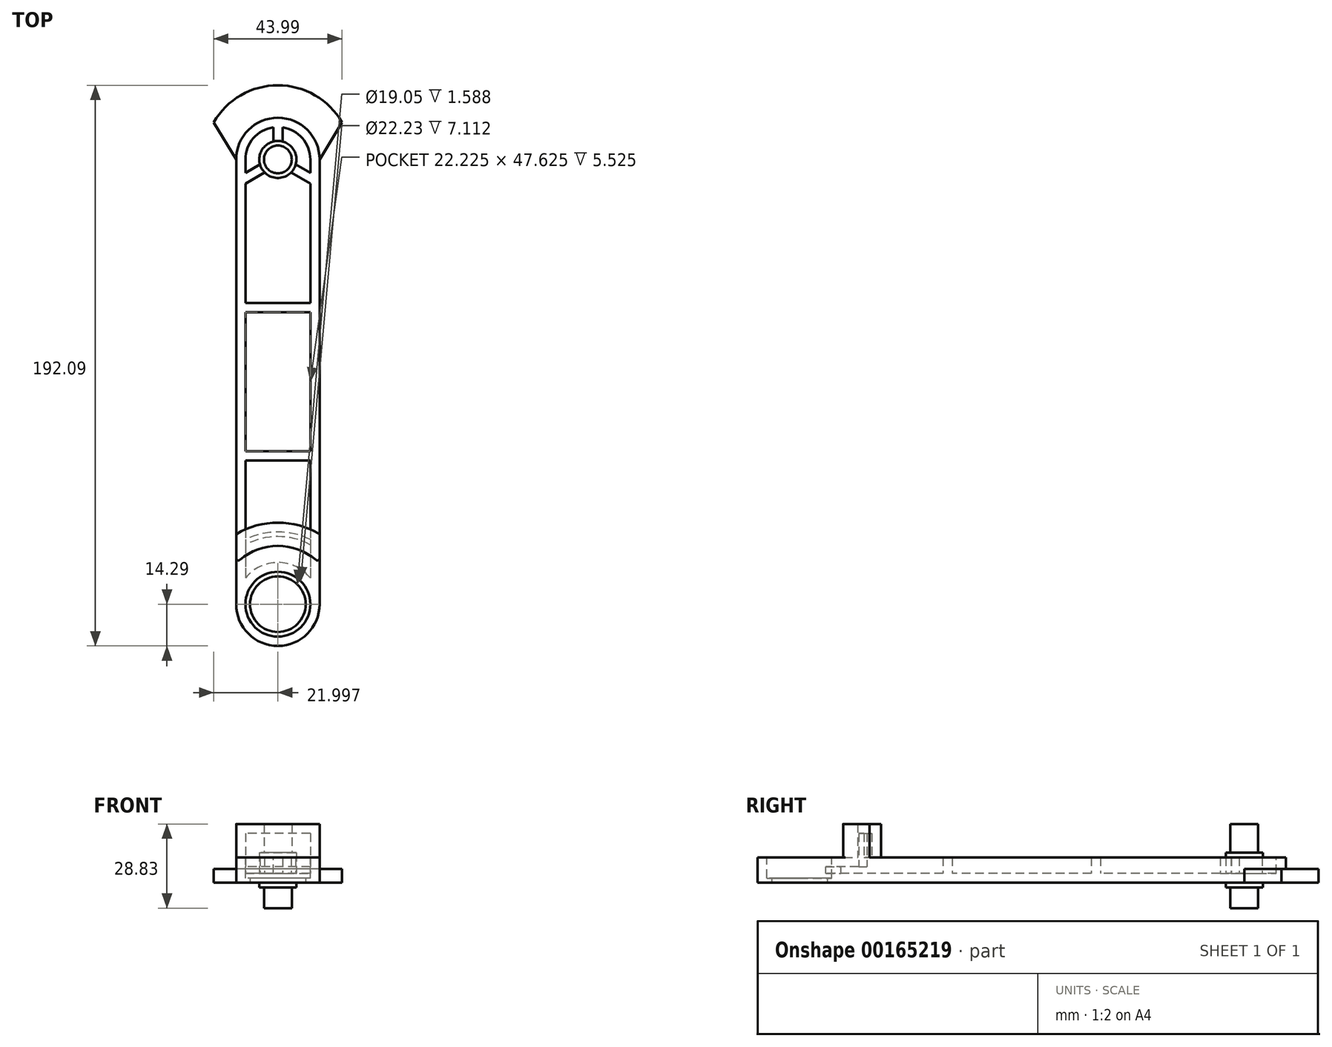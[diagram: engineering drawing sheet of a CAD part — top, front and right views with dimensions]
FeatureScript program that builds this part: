
annotation { "Feature Type Name" : "Feature", "Feature Type Description" : "" }
export const myFeature = defineFeature(function(context is Context, id is Id, definition is map)
    precondition{}
    {
        {
            var Q0;
            Q0=qCreatedBy(makeId("Top.planeOp"),FACE);
            var sketch = newSketch(context, id + "F0", { "sketchPlane" : qUnion([Q0])});
            skLineSegment(sketch, "E0.bottom", {"start": v(0, 0) * mm, "end": v(28.58, 0) * mm, "construction": true});
            skLineSegment(sketch, "E0.top", {"start": v(0, -152.4) * mm, "end": v(28.58, -152.4) * mm, "construction": true});
            skLineSegment(sketch, "E0.left", {"start": v(0, 0) * mm, "end": v(0, -152.4) * mm});
            skLineSegment(sketch, "E0.right", {"start": v(28.58, 0) * mm, "end": v(28.58, -152.4) * mm});
            skArc(sketch, "E1", {"start": v(0, -152.4) * mm, "mid": v(14.29, -166.69) * mm, "end": v(28.58, -152.4) * mm});
            skCircle(sketch, "E2", {"center": v(14.29, -152.4) * mm, "radius": 9.53 * mm});
            skLineSegment(sketch, "E3", {"start": v(0, 0) * mm, "end": v(-7.7, 12.7) * mm});
            skLineSegment(sketch, "E4", {"start": v(-7.7, 12.7) * mm, "end": v(36.28, 12.7) * mm, "construction": true});
            skLineSegment(sketch, "E5", {"start": v(36.28, 12.7) * mm, "end": v(28.57, 0) * mm});
            skLineSegment(sketch, "E6", {"start": v(14.29, 0) * mm, "end": v(14.29, 12.7) * mm, "construction": true});
            skArc(sketch, "E7", {"start": v(36.28, 12.7) * mm, "mid": v(14.29, 25.4) * mm, "end": v(-7.7, 12.7) * mm});
            skLineSegment(sketch, "E8", {"start": v(-7.7, 12.7) * mm, "end": v(14.29, 0) * mm, "construction": true});
            skLineSegment(sketch, "E9", {"start": v(14.29, 0) * mm, "end": v(36.28, 12.7) * mm, "construction": true});
            skSolve(sketch);
        }
        {
            var Q0;
            Q0 = qSketchRegion(id + "F0", true);
            extrude(context, id + "F1", {"entities" : qUnion([Q0]), "depth" : 8.7 * mm});
        }
        {
            var Q0;
            Q0=makeQuery(id+"F1.opExtrude","CAP_FACE",FACE,{"disambiguationData":[OSD([sQuery(id+"F0.wireOp",EDGE,"E0.left"),sQuery(id+"F0.wireOp",EDGE,"E0.right"),sQuery(id+"F0.wireOp",EDGE,"E1"),sQuery(id+"F0.wireOp",EDGE,"bbfeQyJU-4Eoz-mEa2-qj02-75LyADXawIuP"),sQuery(id+"F0.wireOp",EDGE,"E2")])],"isStart":false});
            var sketch = newSketch(context, id + "F2", { "sketchPlane" : qUnion([Q0])});
            skCircle(sketch, "E10", {"center": v(14.29, -152.4) * mm, "radius": 11.11 * mm});
            skSolve(sketch);
        }
        {
            var Q0;
            Q0 = qSketchRegion(id + "F2", true);
            extrude(context, id + "F3", {"entities" : qUnion([Q0]), "operationType" : NewBodyOperationType.REMOVE, "oppositeDirection" : true, "depth" : 7.11 * mm});
        }
        {
            var Q0;
            Q0=makeQuery(id+"F1.opExtrude","CAP_FACE",FACE,{"disambiguationData":[OSD([sQuery(id+"F0.wireOp",EDGE,"E0.left"),sQuery(id+"F0.wireOp",EDGE,"E0.right"),sQuery(id+"F0.wireOp",EDGE,"E1"),sQuery(id+"F0.wireOp",EDGE,"bbfeQyJU-4Eoz-mEa2-qj02-75LyADXawIuP"),sQuery(id+"F0.wireOp",EDGE,"E2")])],"isStart":false});
            var sketch = newSketch(context, id + "F4", { "sketchPlane" : qUnion([Q0])});
            skArc(sketch, "E11", {"start": v(28.57, -138.4) * mm, "mid": v(14.29, -132.39) * mm, "end": v(0, -138.4) * mm});
            skArc(sketch, "E12", {"start": v(28.58, -128.38) * mm, "mid": v(14.29, -124.45) * mm, "end": v(0, -128.38) * mm});
            skLineSegment(sketch, "E13", {"start": v(0, -128.38) * mm, "end": v(0, -138.4) * mm});
            skLineSegment(sketch, "E14", {"start": v(28.58, -128.38) * mm, "end": v(28.58, -138.4) * mm});
            skSolve(sketch);
        }
        {
            var Q0;
            Q0=makeQuery(id+"F4.imprint","IMPRINT",FACE,{"disambiguationData":[TD([[makeQuery(id+"F4.imprint","IMPRINT",EDGE,{"derivedFrom":sQuery(id+"F4.wireOp",EDGE,"E11")}),-1.0]])]});
            extrude(context, id + "F5", {"entities" : qUnion([Q0]), "operationType" : NewBodyOperationType.ADD, "depth" : 11.43 * mm});
        }
        {
            var Q0;
            Q0=makeQuery(id+"F5.opExtrude","SWEPT_EDGE",EDGE,{"disambiguationData":[OSD([sQuery(id+"F0.wireOp",EDGE,"E0.left"),sQuery(id+"F4.wireOp",EDGE,"E11"),sQuery(id+"F4.wireOp",EDGE,"E13")])]});
            var Q1;
            Q1=makeQuery(id+"F5.opExtrude","SWEPT_EDGE",EDGE,{"disambiguationData":[OSD([sQuery(id+"F0.wireOp",EDGE,"E0.right"),sQuery(id+"F4.wireOp",EDGE,"E11"),sQuery(id+"F4.wireOp",EDGE,"E14")])]});
            fillet(context, id + "F6", {"entities" : qUnion([Q0, Q1]), "radius" : 0.76 * mm, "tangentPropagation" : true, "allowEdgeOverflow" : false});
        }
        {
            var Q0;
            Q0=makeQuery(id+"F1.opExtrude","CAP_FACE",FACE,{"disambiguationData":[OSD([sQuery(id+"F0.wireOp",EDGE,"E0.left"),sQuery(id+"F0.wireOp",EDGE,"E0.right"),sQuery(id+"F0.wireOp",EDGE,"E1"),sQuery(id+"F0.wireOp",EDGE,"E2"),sQuery(id+"F0.wireOp",EDGE,"E3"),sQuery(id+"F0.wireOp",EDGE,"E5"),sQuery(id+"F0.wireOp",EDGE,"E7")])],"isStart":true});
            var sketch = newSketch(context, id + "F7", { "sketchPlane" : qUnion([Q0])});
            skCircle(sketch, "E15", {"center": v(14.29, 0) * mm, "radius": 6.35 * mm});
            skSolve(sketch);
        }
        {
            var Q0;
            Q0 = qSketchRegion(id + "F7", true);
            extrude(context, id + "F8", {"entities" : qUnion([Q0]), "operationType" : NewBodyOperationType.ADD, "depth" : 1.59 * mm});
        }
        {
            var Q0;
            Q0=makeQuery(id+"F8.opExtrude","CAP_FACE",FACE,{"disambiguationData":[OSD([sQuery(id+"F7.wireOp",EDGE,"E15")])],"isStart":false});
            var sketch = newSketch(context, id + "F9", { "sketchPlane" : qUnion([Q0])});
            skCircle(sketch, "E16", {"center": v(14.29, 0) * mm, "radius": 4.76 * mm});
            skSolve(sketch);
        }
        {
            var Q0;
            Q0 = qSketchRegion(id + "F9", true);
            extrude(context, id + "F10", {"entities" : qUnion([Q0]), "operationType" : NewBodyOperationType.ADD, "depth" : 7.11 * mm});
        }
        {
            var Q0;
            {var subQ0=sQuery(id+"F0.wireOp",EDGE,"E5");var subQ1=sQuery(id+"F0.wireOp",EDGE,"E3");var subQ2=sQuery(id+"F0.wireOp",EDGE,"E0.right");var subQ3=sQuery(id+"F0.wireOp",EDGE,"E0.left");var subQ4=sQuery(id+"F0.wireOp",EDGE,"E7");Q0=makeQuery(id+"F5.boolean.opBoolean","SPLIT",FACE,{"disambiguationData":[TD([makeQuery(id+"F1.opExtrude","SWEPT_FACE",FACE,{"disambiguationData":[OSD([subQ1])]})])],"derivedFrom":makeQuery(id+"F1.opExtrude","CAP_FACE",FACE,{"disambiguationData":[OSD([subQ3,subQ2,sQuery(id+"F0.wireOp",EDGE,"E1"),sQuery(id+"F0.wireOp",EDGE,"E2"),subQ1,subQ0,subQ4])],"isStart":false})});}
            var sketch = newSketch(context, id + "F11", { "sketchPlane" : qUnion([Q0])});
            skArc(sketch, "E17", {"start": v(28.57, 0) * mm, "mid": v(14.29, 14.29) * mm, "end": v(0, 0) * mm});
            skSolve(sketch);
        }
        {
            var Q0;
            Q0 = qSketchRegion(id + "F11", true);
            var Q1;
            Q1=makeQuery(id+"F11.imprint","IMPRINT",FACE,{"disambiguationData":[TD([[makeQuery(id+"F11.imprint","IMPRINT",EDGE,{"derivedFrom":sQuery(id+"F11.wireOp",EDGE,"E17")}),-1.0]])]});
            extrude(context, id + "F12", {"entities" : qUnion([Q0, Q1]), "operationType" : NewBodyOperationType.REMOVE, "oppositeDirection" : true, "depth" : 3.94 * mm});
        }
        {
            var Q0;
            {var subQ0=sQuery(id+"F0.wireOp",EDGE,"E5");var subQ1=sQuery(id+"F0.wireOp",EDGE,"E3");var subQ2=sQuery(id+"F0.wireOp",EDGE,"E0.right");var subQ3=sQuery(id+"F0.wireOp",EDGE,"E0.left");var subQ4=sQuery(id+"F0.wireOp",EDGE,"E7");Q0=makeQuery(id+"F5.boolean.opBoolean","SPLIT",FACE,{"disambiguationData":[TD([makeQuery(id+"F1.opExtrude","SWEPT_FACE",FACE,{"disambiguationData":[OSD([subQ1])]})])],"derivedFrom":makeQuery(id+"F1.opExtrude","CAP_FACE",FACE,{"disambiguationData":[OSD([subQ3,subQ2,sQuery(id+"F0.wireOp",EDGE,"E1"),sQuery(id+"F0.wireOp",EDGE,"E2"),subQ1,subQ0,subQ4])],"isStart":false})});}
            shell(context, id + "F13", {"entities" : qUnion([Q0]), "thickness" : 3.17 * mm});
        }
        {
            var Q0;
            {var subQ0=sQuery(id+"F9.wireOp",EDGE,"E16");Q0=makeQuery(id+"F13.opShell","OFFSET_FACE",FACE,{"disambiguationData":[OSD([subQ0]),TDD([makeQuery(id+"F10.opExtrude","CAP_FACE",FACE,{"disambiguationData":[OSD([subQ0])],"isStart":false})])]});}
            var sketch = newSketch(context, id + "F14", { "sketchPlane" : qUnion([Q0])});
            skCircle(sketch, "E18", {"center": v(14.29, 0) * mm, "radius": 4.76 * mm});
            skSolve(sketch);
        }
        {
            var Q0;
            Q0 = qSketchRegion(id + "F14", true);
            var Q1;
            Q1=makeQuery(id+"F5.opExtrude","CAP_FACE",FACE,{"disambiguationData":[OSD([sQuery(id+"F4.wireOp",EDGE,"E11"),sQuery(id+"F4.wireOp",EDGE,"E12"),sQuery(id+"F4.wireOp",EDGE,"E13"),sQuery(id+"F4.wireOp",EDGE,"E14")])],"isStart":false});
            extrude(context, id + "F15", {"entities" : qUnion([Q0]), "operationType" : NewBodyOperationType.ADD, "endBound" : BoundingType.UP_TO_SURFACE, "endBoundEntityFace" : qUnion([Q1]), "depth" : 25.4 * mm});
        }
        {
            var Q0;
            {var subQ0=sQuery(id+"F0.wireOp",EDGE,"E7");var subQ1=sQuery(id+"F0.wireOp",EDGE,"E5");var subQ2=sQuery(id+"F0.wireOp",EDGE,"E3");var subQ3=sQuery(id+"F0.wireOp",EDGE,"E2");var subQ4=sQuery(id+"F0.wireOp",EDGE,"E1");var subQ5=sQuery(id+"F0.wireOp",EDGE,"E0.right");var subQ6=sQuery(id+"F0.wireOp",EDGE,"E0.left");Q0=makeQuery(id+"F13.opShell","OFFSET_FACE",FACE,{"disambiguationData":[OSD([subQ6,subQ5,subQ4,subQ3,subQ2,subQ1,subQ0]),TDD([makeQuery(id+"F1.opExtrude","CAP_FACE",FACE,{"disambiguationData":[OSD([subQ6,subQ5,subQ4,subQ3,subQ2,subQ1,subQ0])],"isStart":true})])]});}
            var sketch = newSketch(context, id + "F16", { "sketchPlane" : qUnion([Q0])});
            skCircle(sketch, "E19", {"center": v(14.29, 0) * mm, "radius": 6.35 * mm});
            skSolve(sketch);
        }
        {
            var Q0;
            Q0 = qSketchRegion(id + "F16", true);
            extrude(context, id + "F17", {"entities" : qUnion([Q0]), "operationType" : NewBodyOperationType.ADD, "depth" : 7.11 * mm});
        }
        {
            var Q0;
            {var subQ0=sQuery(id+"F0.wireOp",EDGE,"E7");var subQ1=sQuery(id+"F0.wireOp",EDGE,"E5");var subQ2=sQuery(id+"F0.wireOp",EDGE,"E3");var subQ3=sQuery(id+"F0.wireOp",EDGE,"E2");var subQ4=sQuery(id+"F0.wireOp",EDGE,"E1");var subQ5=sQuery(id+"F0.wireOp",EDGE,"E0.right");var subQ6=sQuery(id+"F0.wireOp",EDGE,"E0.left");Q0=makeQuery(id+"F13.opShell","OFFSET_FACE",FACE,{"disambiguationData":[OSD([subQ6,subQ5,subQ4,subQ3,subQ2,subQ1,subQ0]),TDD([makeQuery(id+"F1.opExtrude","CAP_FACE",FACE,{"disambiguationData":[OSD([subQ6,subQ5,subQ4,subQ3,subQ2,subQ1,subQ0])],"isStart":true})])]});}
            var sketch = newSketch(context, id + "F18", { "sketchPlane" : qUnion([Q0])});
            skLineSegment(sketch, "E20", {"start": v(14.29, 0) * mm, "end": v(23.91, -5.56) * mm, "construction": true});
            skLineSegment(sketch, "E21", {"start": v(23.91, -5.56) * mm, "end": v(14.29, 11.11) * mm, "construction": true});
            skLineSegment(sketch, "E22", {"start": v(14.29, 11.11) * mm, "end": v(14.29, 0) * mm, "construction": true});
            skLineSegment(sketch, "E23", {"start": v(14.29, 0) * mm, "end": v(4.66, -5.56) * mm, "construction": true});
            skLineSegment(sketch, "E24", {"start": v(4.66, -5.56) * mm, "end": v(23.91, -5.56) * mm, "construction": true});
            skLineSegment(sketch, "E25", {"start": v(14.29, 11.11) * mm, "end": v(4.66, -5.56) * mm, "construction": true});
            skLineSegment(sketch, "E26.bottom", {"start": v(15.87, 11.11) * mm, "end": v(12.7, 11.11) * mm});
            skLineSegment(sketch, "E26.top", {"start": v(15.87, 0) * mm, "end": v(12.7, 0) * mm});
            skLineSegment(sketch, "E26.left", {"start": v(15.87, 11.11) * mm, "end": v(15.87, 0) * mm});
            skLineSegment(sketch, "E26.right", {"start": v(12.7, 11.11) * mm, "end": v(12.7, 0) * mm});
            skPoint(sketch, "E26.middle", {"position": v(14.29, 5.56) * mm});
            skLineSegment(sketch, "E27.bottom", {"start": v(15.78, 2.7) * mm, "end": v(17.36, -0.06) * mm});
            skLineSegment(sketch, "E27.top", {"start": v(1.59, -5.5) * mm, "end": v(3.18, -8.25) * mm});
            skLineSegment(sketch, "E27.left", {"start": v(15.78, 2.7) * mm, "end": v(1.59, -5.5) * mm});
            skLineSegment(sketch, "E27.right", {"start": v(17.36, -0.06) * mm, "end": v(3.18, -8.25) * mm});
            skPoint(sketch, "E27.middle", {"position": v(9.48, -2.78) * mm});
            skLineSegment(sketch, "E28.bottom", {"start": v(26.99, -5.5) * mm, "end": v(25.4, -8.25) * mm});
            skLineSegment(sketch, "E28.top", {"start": v(12.8, 2.7) * mm, "end": v(11.21, -0.06) * mm});
            skLineSegment(sketch, "E28.left", {"start": v(26.99, -5.5) * mm, "end": v(12.8, 2.7) * mm});
            skLineSegment(sketch, "E28.right", {"start": v(25.4, -8.25) * mm, "end": v(11.21, -0.06) * mm});
            skPoint(sketch, "E28.middle", {"position": v(19.1, -2.78) * mm});
            skLineSegment(sketch, "E29", {"start": v(14.29, 0) * mm, "end": v(14.29, -50.8) * mm, "construction": true});
            skLineSegment(sketch, "E30", {"start": v(14.29, -50.8) * mm, "end": v(14.29, -101.6) * mm, "construction": true});
            skLineSegment(sketch, "E31", {"start": v(14.29, -101.6) * mm, "end": v(14.29, -152.4) * mm, "construction": true});
            skLineSegment(sketch, "E32.bottom", {"start": v(3.18, -52.39) * mm, "end": v(25.4, -52.39) * mm});
            skLineSegment(sketch, "E32.top", {"start": v(3.18, -49.21) * mm, "end": v(25.4, -49.21) * mm});
            skLineSegment(sketch, "E32.left", {"start": v(3.18, -52.39) * mm, "end": v(3.18, -49.21) * mm});
            skLineSegment(sketch, "E32.right", {"start": v(25.4, -52.39) * mm, "end": v(25.4, -49.21) * mm});
            skPoint(sketch, "E32.middle", {"position": v(14.29, -50.8) * mm});
            skLineSegment(sketch, "E33.bottom", {"start": v(3.18, -100.01) * mm, "end": v(25.4, -100.01) * mm});
            skLineSegment(sketch, "E33.top", {"start": v(3.18, -103.19) * mm, "end": v(25.4, -103.19) * mm});
            skLineSegment(sketch, "E33.left", {"start": v(3.18, -100.01) * mm, "end": v(3.18, -103.19) * mm});
            skLineSegment(sketch, "E33.right", {"start": v(25.4, -100.01) * mm, "end": v(25.4, -103.19) * mm});
            skPoint(sketch, "E33.middle", {"position": v(14.29, -101.6) * mm});
            skSolve(sketch);
        }
        {
            var Q0;
            Q0 = qSketchRegion(id + "F18", true);
            var Q1;
            {var subQ0=sQuery(id+"F0.wireOp",EDGE,"E5");var subQ1=sQuery(id+"F0.wireOp",EDGE,"E3");var subQ2=sQuery(id+"F0.wireOp",EDGE,"E0.right");var subQ3=sQuery(id+"F0.wireOp",EDGE,"E0.left");var subQ4=sQuery(id+"F0.wireOp",EDGE,"E7");Q1=makeQuery(id+"F5.boolean.opBoolean","SPLIT",FACE,{"disambiguationData":[TD([makeQuery(id+"F1.opExtrude","SWEPT_FACE",FACE,{"disambiguationData":[OSD([subQ1])]})])],"derivedFrom":makeQuery(id+"F1.opExtrude","CAP_FACE",FACE,{"disambiguationData":[OSD([subQ3,subQ2,sQuery(id+"F0.wireOp",EDGE,"E1"),sQuery(id+"F0.wireOp",EDGE,"E2"),subQ1,subQ0,subQ4])],"isStart":false})});}
            extrude(context, id + "F19", {"entities" : qUnion([Q0]), "operationType" : NewBodyOperationType.ADD, "endBound" : BoundingType.UP_TO_SURFACE, "endBoundEntityFace" : qUnion([Q1]), "depth" : 25.4 * mm});
        }
    });
